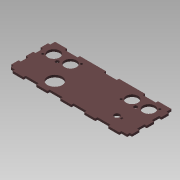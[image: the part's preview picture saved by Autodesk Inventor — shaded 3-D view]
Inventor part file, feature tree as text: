
AUTODESK INVENTOR PART (.ipt)
format: ipt  version: 2015 SP1 (Build 190203100, 203)  size: 191,488 bytes
history: native  units: mm
features: extrude x1, sketch x1
ambient origin geometry x8: Origin, YZ Plane, XZ Plane, XY Plane, X Axis, Y Axis, Z Axis, Center Point
bodies: Solid1 (feature_tree)
feature tree (2):
  extrude  "Extrusion1"  Depth=15.0mm
  sketch  "Sketch1"  dims[d2=20.0mm d4=15.0mm d5=3.0mm d8=30.0mm d10=32.5mm d11=30.0mm d13=32.5mm d16=1.5mm d17=3.0mm d18=10.0mm d19=20.0mm d21=20.0mm d22=20.0mm d24=20.0mm d27=3.0mm d28=0.0mm]
